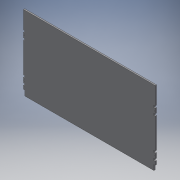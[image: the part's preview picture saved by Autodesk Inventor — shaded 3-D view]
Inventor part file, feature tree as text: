
AUTODESK INVENTOR PART (.ipt)
format: ipt  version: 2019 (Build 230136000, 136)  size: 183,296 bytes
history: native  units: in
note: dims shown in document units (in); Inventor stores cm internally (conversion verified against a paired STEP export)
features: reference x14, extrude x3, sketch x3, other x3, helix x1
ambient origin geometry x8: Origin, YZ Plane, XZ Plane, XY Plane, X Axis, Y Axis, Z Axis, Center Point
bodies: Solid1 (feature_tree)
feature tree (24):
  extrude  "Extrusion1"  Depth=9.0551in
  extrude  "Extrusion4"  Depth=0.1575in
  extrude  "Extrusion5"  Depth=0.0079in
  sketch  "Sketch1"  dims[d0=15.748in d1=9.0551in]
  sketch  "Sketch4"  dims[d2=0.1575in d3=0.0in d31=0.5906in]
  reference  "Reference1"
  reference  "Reference2"
  sketch  "Sketch5"  dims[d50=0.3937in d51=0.0in d52=0.126in d53=0.126in d54=0.126in d55=0.126in d56=0.3937in d57=0.0in d58=0.0079in d59=0.0079in d60=0.0079in d61=0.0079in d62=0.0079in d63=0.0079in d64=0.0079in d65=0.0079in]
  reference  "Reference3"
  reference  "Reference4"
  reference  "Reference5"
  reference  "Reference6"
  reference  "Reference7"
  reference  "Reference8"
  reference  "Reference9"
  reference  "Reference10"
  reference  "Reference11"
  reference  "Reference12"
  reference  "Reference13"
  reference  "Reference14"
  other  "<userpath>\Documents\CAD Files\Helix DLP\Helix DLP Z Stage.iam"
  helix  "Helix DLP Z Stage.iam"  [1 undecoded]
  other  "Z stage_side:2"
  other  "Z stage_side:1"
note: 1 required parameter value undecoded (feature->parameter linkage not recoverable at this tier; creation-order binding heuristic only, values carry confidence <= 0.55)
